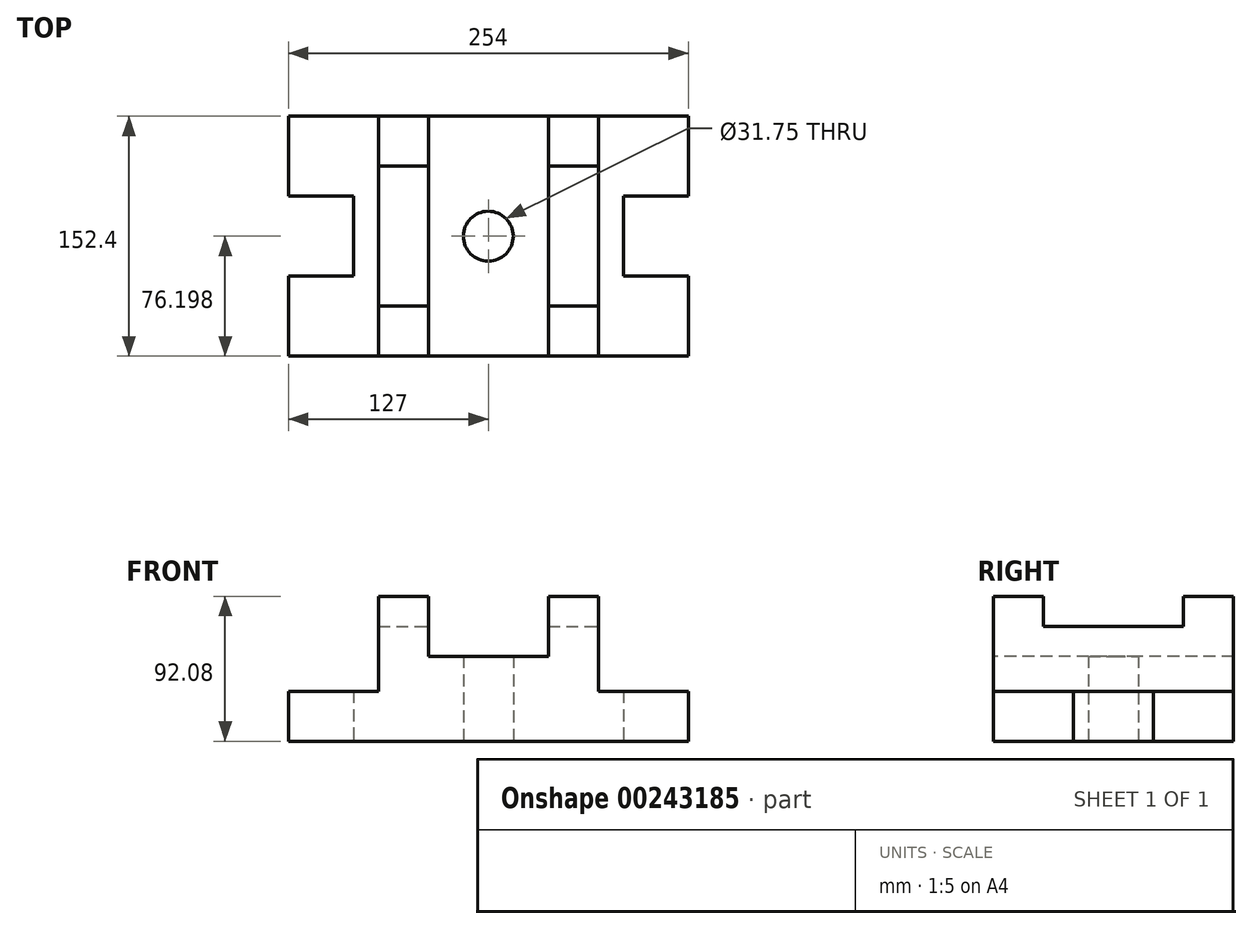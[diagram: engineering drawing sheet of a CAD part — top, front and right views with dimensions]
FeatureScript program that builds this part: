
annotation { "Feature Type Name" : "Feature", "Feature Type Description" : "" }
export const myFeature = defineFeature(function(context is Context, id is Id, definition is map)
    precondition{}
    {
        {
            var Q0;
            Q0=qCreatedBy(makeId("Top.planeOp"),FACE);
            var sketch = newSketch(context, id + "F0", { "sketchPlane" : qUnion([Q0])});
            skLineSegment(sketch, "E0", {"start": v(-159.95, -38.3) * mm, "end": v(94.05, -38.3) * mm});
            skLineSegment(sketch, "E1", {"start": v(94.05, -38.3) * mm, "end": v(94.05, 12.5) * mm});
            skLineSegment(sketch, "E2", {"start": v(94.05, 12.5) * mm, "end": v(52.77, 12.5) * mm});
            skLineSegment(sketch, "E3", {"start": v(52.77, 12.5) * mm, "end": v(52.77, 63.3) * mm});
            skLineSegment(sketch, "E4", {"start": v(52.77, 63.3) * mm, "end": v(94.05, 63.3) * mm});
            skLineSegment(sketch, "E5", {"start": v(94.05, 63.3) * mm, "end": v(94.05, 114.1) * mm});
            skLineSegment(sketch, "E6", {"start": v(94.05, 114.1) * mm, "end": v(-159.95, 114.1) * mm});
            skLineSegment(sketch, "E7", {"start": v(-159.95, 114.1) * mm, "end": v(-159.95, 63.3) * mm});
            skLineSegment(sketch, "E8", {"start": v(-159.95, 63.3) * mm, "end": v(-118.68, 63.3) * mm});
            skLineSegment(sketch, "E9", {"start": v(-118.68, 63.3) * mm, "end": v(-118.68, 12.5) * mm});
            skLineSegment(sketch, "E10", {"start": v(-118.68, 12.5) * mm, "end": v(-159.95, 12.5) * mm});
            skLineSegment(sketch, "E11", {"start": v(-159.95, 12.5) * mm, "end": v(-159.95, -38.3) * mm});
            skPoint(sketch, "E12", {"position": v(36.9, 114.1) * mm});
            skLineSegment(sketch, "E13", {"start": v(36.9, 114.1) * mm, "end": v(36.9, -38.3) * mm});
            skPoint(sketch, "E14", {"position": v(5.15, 114.1) * mm});
            skLineSegment(sketch, "E15", {"start": v(5.15, 114.1) * mm, "end": v(5.15, -38.3) * mm});
            skPoint(sketch, "E16", {"position": v(-71.05, 114.1) * mm});
            skPoint(sketch, "E17", {"position": v(-102.8, 114.1) * mm});
            skLineSegment(sketch, "E18", {"start": v(-71.05, 114.1) * mm, "end": v(-71.05, -38.3) * mm});
            skLineSegment(sketch, "E19", {"start": v(-102.8, 114.1) * mm, "end": v(-102.8, -38.3) * mm});
            skPoint(sketch, "E20", {"position": v(-102.8, 82.36) * mm});
            skPoint(sketch, "E21", {"position": v(-102.8, -6.54) * mm});
            skLineSegment(sketch, "E22", {"start": v(-102.8, 82.36) * mm, "end": v(-71.05, 82.36) * mm});
            skLineSegment(sketch, "E23", {"start": v(-102.8, -6.54) * mm, "end": v(-71.05, -6.54) * mm});
            skPoint(sketch, "E24", {"position": v(5.15, 82.36) * mm});
            skPoint(sketch, "E25", {"position": v(5.15, -6.54) * mm});
            skLineSegment(sketch, "E26", {"start": v(5.15, 82.36) * mm, "end": v(36.9, 82.36) * mm});
            skLineSegment(sketch, "E27", {"start": v(5.15, -6.54) * mm, "end": v(36.9, -6.54) * mm});
            skPoint(sketch, "E28", {"position": v(-32.95, -38.3) * mm});
            skCircle(sketch, "E29", {"center": v(-32.95, 37.9) * mm, "radius": 15.88 * mm});
            skSolve(sketch);
        }
        {
            var Q0;
            {var subQ0=sQuery(id+"F0.wireOp",EDGE,"E7");Q0=makeQuery(id+"F0.imprint","IMPRINT",FACE,{"disambiguationData":[TD([[makeQuery(id+"F0.imprint","IMPRINT",EDGE,{"derivedFrom":subQ0}),1.0]])]});}
            var Q1;
            {var subQ0=sQuery(id+"F0.wireOp",EDGE,"E1");Q1=makeQuery(id+"F0.imprint","IMPRINT",FACE,{"disambiguationData":[TD([[makeQuery(id+"F0.imprint","IMPRINT",EDGE,{"derivedFrom":subQ0}),1.0]])]});}
            extrude(context, id + "F1", {"entities" : qUnion([Q0, Q1]), "depth" : 31.75 * mm});
        }
        {
            var Q0;
            Q0=makeQuery(id+"F0.imprint","IMPRINT",FACE,{"disambiguationData":[TD([[makeQuery(id+"F0.imprint","IMPRINT",EDGE,{"derivedFrom":sQuery(id+"F0.wireOp",EDGE,"E29")}),-1.0]])]});
            extrude(context, id + "F2", {"entities" : qUnion([Q0]), "operationType" : NewBodyOperationType.ADD, "depth" : 53.97 * mm});
        }
        {
            var Q0;
            {var subQ5=sQuery(id+"F0.wireOp",EDGE,"E22");Q0=makeQuery(id+"F0.imprint","IMPRINT",FACE,{"disambiguationData":[TD([[makeQuery(id+"F0.imprint","IMPRINT",EDGE,{"derivedFrom":subQ5}),1.0]])]});}
            var Q1;
            {var subQ5=sQuery(id+"F0.wireOp",EDGE,"E26");Q1=makeQuery(id+"F0.imprint","IMPRINT",FACE,{"disambiguationData":[TD([[makeQuery(id+"F0.imprint","IMPRINT",EDGE,{"derivedFrom":subQ5}),1.0]])]});}
            var Q2;
            {var subQ5=sQuery(id+"F0.wireOp",EDGE,"E23");Q2=makeQuery(id+"F0.imprint","IMPRINT",FACE,{"disambiguationData":[TD([[makeQuery(id+"F0.imprint","IMPRINT",EDGE,{"derivedFrom":subQ5}),-1.0]])]});}
            var Q3;
            {var subQ5=sQuery(id+"F0.wireOp",EDGE,"E27");Q3=makeQuery(id+"F0.imprint","IMPRINT",FACE,{"disambiguationData":[TD([[makeQuery(id+"F0.imprint","IMPRINT",EDGE,{"derivedFrom":subQ5}),-1.0]])]});}
            extrude(context, id + "F3", {"entities" : qUnion([Q0, Q1, Q2, Q3]), "operationType" : NewBodyOperationType.ADD, "depth" : 92.07 * mm});
        }
        {
            var Q0;
            {var subQ0=sQuery(id+"F0.wireOp",EDGE,"E22");Q0=makeQuery(id+"F0.imprint","IMPRINT",FACE,{"disambiguationData":[TD([[makeQuery(id+"F0.imprint","IMPRINT",EDGE,{"derivedFrom":subQ0}),-1.0]])]});}
            var Q1;
            {var subQ0=sQuery(id+"F0.wireOp",EDGE,"E26");Q1=makeQuery(id+"F0.imprint","IMPRINT",FACE,{"disambiguationData":[TD([[makeQuery(id+"F0.imprint","IMPRINT",EDGE,{"derivedFrom":subQ0}),-1.0]])]});}
            extrude(context, id + "F4", {"entities" : qUnion([Q0, Q1]), "operationType" : NewBodyOperationType.ADD, "depth" : 73.02 * mm});
        }
    });
